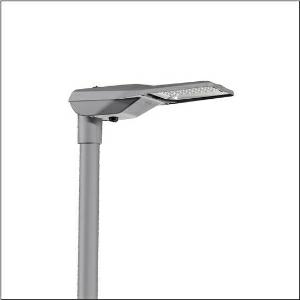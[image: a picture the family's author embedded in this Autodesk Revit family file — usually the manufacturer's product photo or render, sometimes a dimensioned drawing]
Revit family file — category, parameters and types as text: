
# Revit family: streetlight_sl_21_iq_mini___st1_0a_5xe2d51y08gb_2a2c
name_source: partatom
category: Lighting Fixtures
units: mm (PartAtom-declared; Revit-internal decimal feet)

## family parameters
Cut with Voids When Loaded = No
Host = Face
Light Source = No
Part Type = Normal
Room Calculation Point = No
Round Connector Dimension = Use Diameter
Shared = No

## types (1)
- --- (1 x LED, 5260 lm, 39.8 W, 3000K)
    Apparent Load = 40 VA
    CIE Flux Codes = 37 72 97 100 100
    Color Rendering = 80
    Color Temperature = 3000K
    Default Elevation = 1800 mm
    Description = Streetlight SL 21 iQ mini, mast luminaire, primary light control with lens, of PMMA, primary optical cover: cover, of toughened safety glass, transparent, light distribution: ST1.0a, light emission: direct distribution, primary light characteristic: asymmetric, installation type: post-top, side-entry, LED, High Power LED, rated luminous flux: 5.260lm, luminous efficacy: 132lm/W, light colour: 830, colour temperature: 3000K, control gear: iQ-Street Remote, D4i with power reduction, control: pre-setting: logarithmic dimming characteristic, Street-Remote, Auto-Match, Temp-Guard, Lumen-Switch, Night-Set, Smart-Wire, Light-Fading, Desk-Remote (wireless, voltage-free reading and setting of iQ features in the workshop via application-optimized NFC function/RFID function), optimised constant luminous flux control (CLO 2.0), mains connection: 220..240V, AC, 50/60Hz, start of lifetime: 40W, end of service life: 41W, reduction: 18W, luminaire housing, of diecast aluminium, powder-coated, Siteco® metallic grey (DB 702S), corrosivity category C5 mid according to DIN EN ISO 12944, please order mast flange separately, inclination adjustable: 0°, 5°, 10°, 15°, sealing non-destructively replaceable, multi-level sealing system, length: 628mm, width: 235mm, height: 110mm, mast flange for spigot size: 42mm (side-entry): 5XC10008XM4, 60/48mm (side-entry/post-top): 5XC10108XM2, 76/60mm (side-entry/post-top): 5XC10108XM1, mounting height: 4..8m, Smart Interface below and above, protection rating (complete): IP66, insulation class (complete): insulation class II (safety insulation), certification: CE, ENEC, ENEC+, VDE, impact resistance: IK10, permissible operating ambient temperature for outdoor applications: -40..+50°C, standard-compliant lighting for roads and squares, packaging unit: 1 piece

Light Distribution: ST1.0a
    Height = 110 mm
    Lamp = 1 x LED
    Lamp Light Flux = 5260 lm
    Lamp Power = 39.8 W
    Lamp count = 1
    Length = 625 mm
    Luminous efficacy = 132 lm/W
    Manufacturer = Siteco
    ModVariant = No
    Model = 5XE2D51Y08GB
    Number of Poles = 1
    OnlyDefault = Yes
    Power Factor = 1
    Product Name = Streetlight SL 21 iQ mini | ST1.0a
    Product group = mast luminaire | pylon top
    ProductGroupID = 6100
    Protection Class = Protection class II
    Protection Degree = IP 66
    RLX_Detail_Level = 1
    RLX_Emergency_Light_Flux = 0 lm
    RLX_Emergency_Type = 0
    RLX_Emergency_Type_DB = No
    RlxData = <blob elided: 92649 chars, md5=17057edc>
    Socket = socket
    Standby Power = 0 W
    System Light Flux = 5260 lm
    System Power = 40 W
    Type Comments = factory setting: luminous flux: 100 % | dim-lin: 254 | 800 mA
    Type Image = l_1003514.jpg
    URL = http://relux.com
    VarID = @adj_136313
    Voltage = 0 V
    Weight = 0.00 kg
    Width = 234 mm

## geometry (parser evidence)
native form markers: Blend x4, Sweep x12
no freeform markers — native parametric forms only
